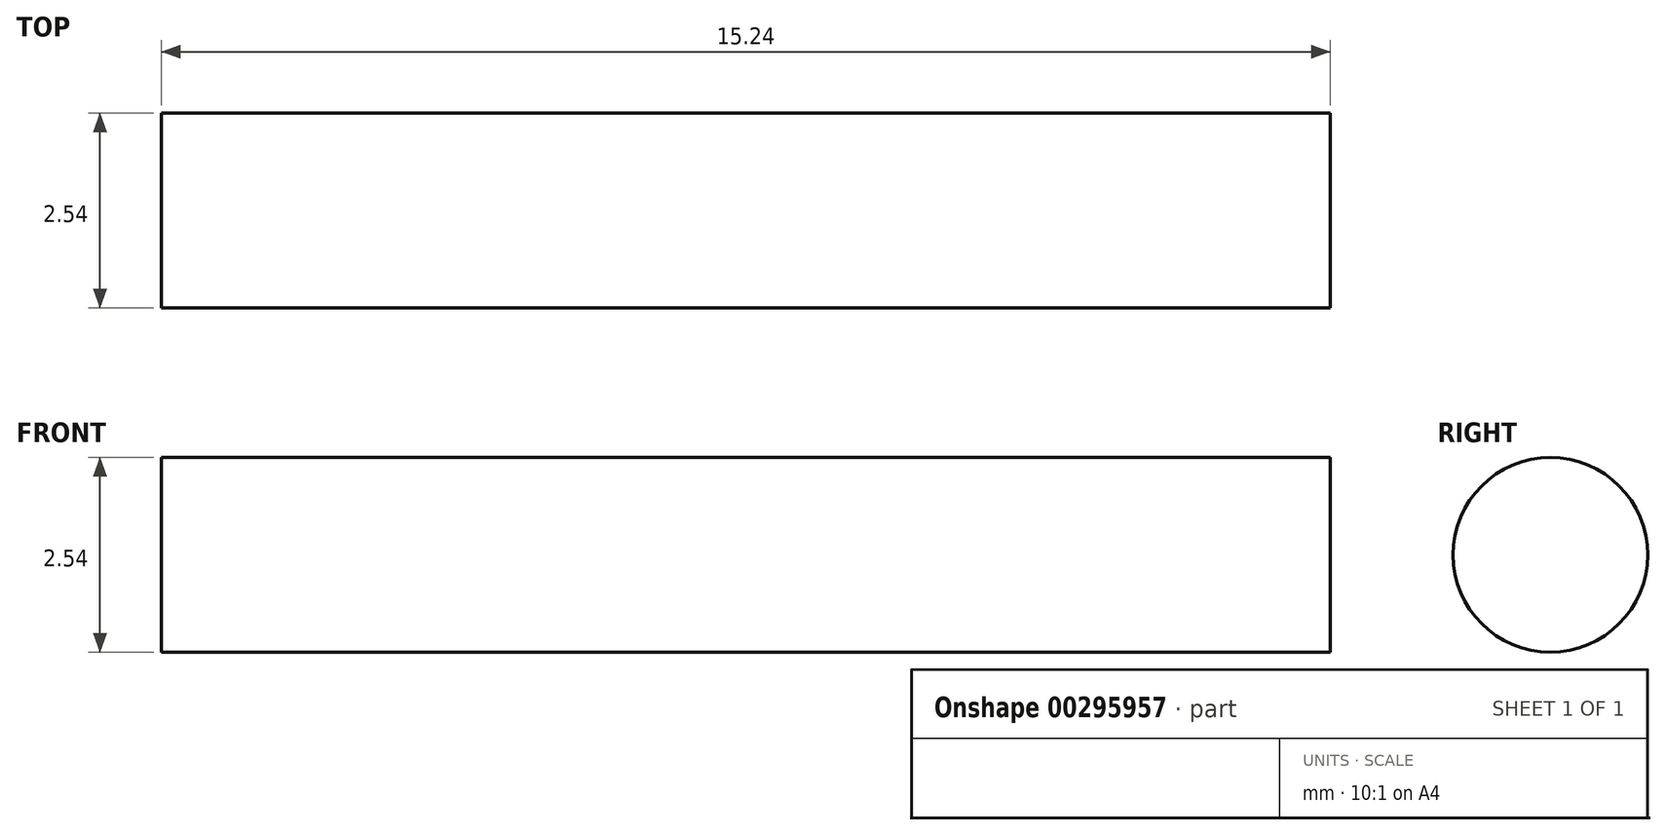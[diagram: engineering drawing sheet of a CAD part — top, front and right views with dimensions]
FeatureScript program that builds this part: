
annotation { "Feature Type Name" : "Feature", "Feature Type Description" : "" }
export const myFeature = defineFeature(function(context is Context, id is Id, definition is map)
    precondition{}
    {
        {
            var Q0;
            Q0=qCreatedBy(makeId("Right.planeOp"),FACE);
            var sketch = newSketch(context, id + "F0", { "sketchPlane" : qUnion([Q0])});
            skCircle(sketch, "E0", {"center": v(0, 0) * mm, "radius": 1.27 * mm});
            skSolve(sketch);
        }
        {
            var Q0;
            Q0 = qSketchRegion(id + "F0", true);
            extrude(context, id + "F1", {"entities" : qUnion([Q0]), "depth" : 15.24 * mm});
        }
    });
